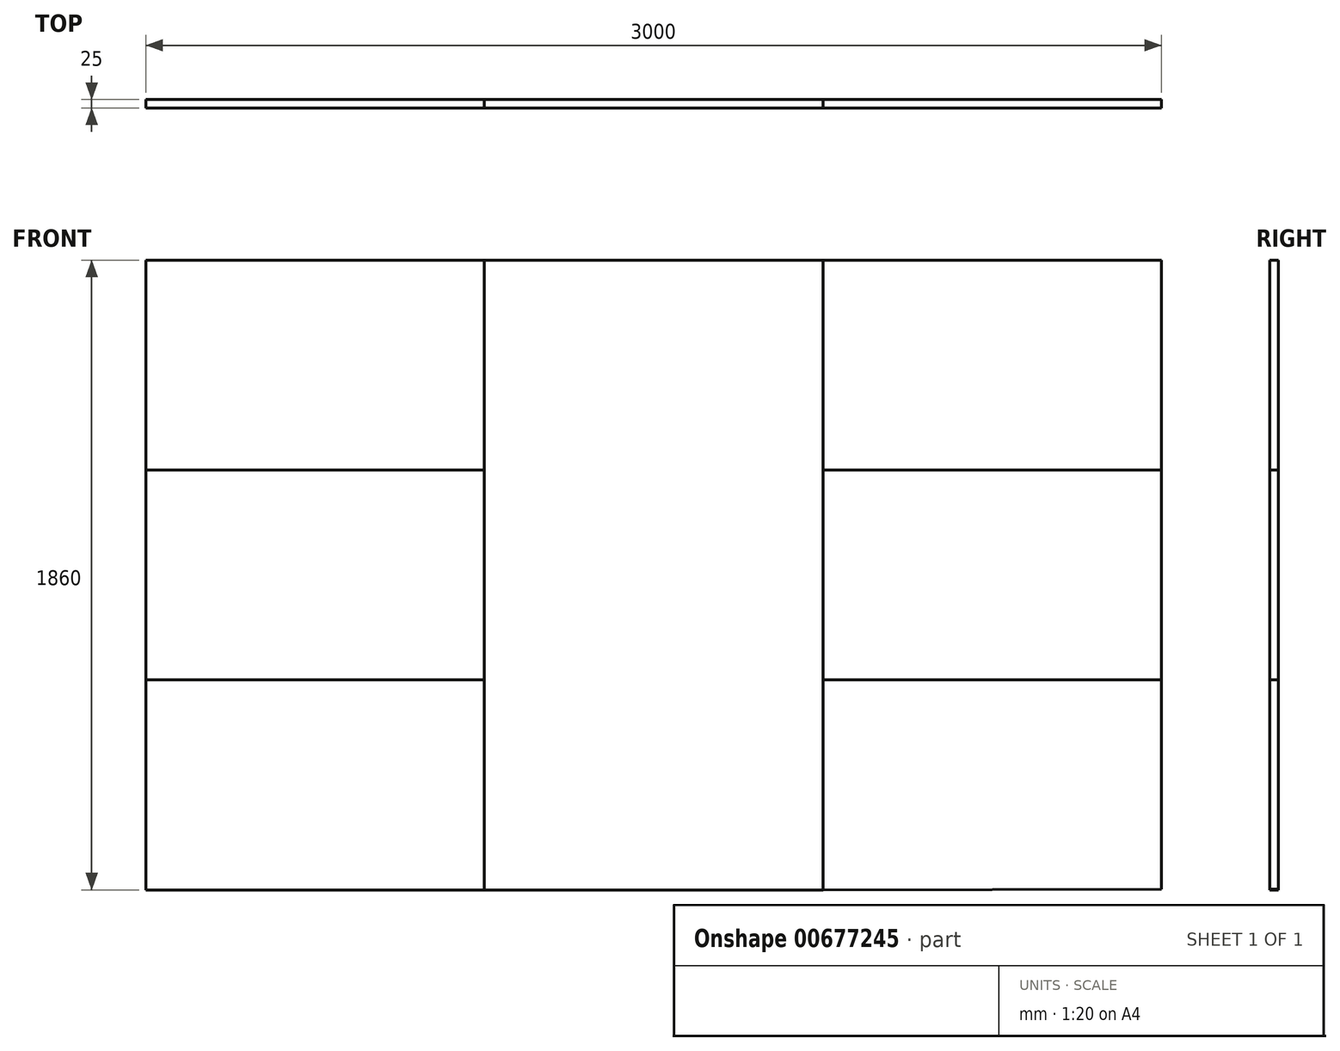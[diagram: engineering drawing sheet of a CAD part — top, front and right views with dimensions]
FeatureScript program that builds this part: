
annotation { "Feature Type Name" : "Feature", "Feature Type Description" : "" }
export const myFeature = defineFeature(function(context is Context, id is Id, definition is map)
    precondition{}
    {
        {
            var Q0;
            Q0=qCreatedBy(makeId("Front.planeOp"),FACE);
            var sketch = newSketch(context, id + "F0", { "sketchPlane" : qUnion([Q0])});
            skLineSegment(sketch, "E0.bottom", {"start": v(-857.14, 930) * mm, "end": v(1142.86, 930) * mm});
            skLineSegment(sketch, "E0.top", {"start": v(-857.14, -930) * mm, "end": v(1142.86, -930) * mm});
            skLineSegment(sketch, "E0.left", {"start": v(-857.14, 930) * mm, "end": v(-857.14, -930) * mm});
            skLineSegment(sketch, "E0.right", {"start": v(1142.86, 930) * mm, "end": v(1142.86, -930) * mm});
            skLineSegment(sketch, "E1", {"start": v(142.86, 930) * mm, "end": v(142.86, -930) * mm});
            skLineSegment(sketch, "E2", {"start": v(-857.14, 310) * mm, "end": v(142.86, 310) * mm});
            skLineSegment(sketch, "E3", {"start": v(-857.14, -310) * mm, "end": v(142.86, -310) * mm});
            skLineSegment(sketch, "E4", {"start": v(1142.86, 930) * mm, "end": v(2142.86, 930) * mm});
            skLineSegment(sketch, "E5", {"start": v(2142.86, 930) * mm, "end": v(2142.86, -928.17) * mm});
            skLineSegment(sketch, "E6", {"start": v(2142.86, -928.17) * mm, "end": v(1142.86, -930) * mm});
            skLineSegment(sketch, "E7", {"start": v(1142.86, -310) * mm, "end": v(2142.86, -310) * mm});
            skLineSegment(sketch, "E8", {"start": v(1142.86, 310) * mm, "end": v(2142.86, 310) * mm});
            skSolve(sketch);
        }
        {
            var Q0;
            Q0=sQuery(id+"F0.wireOp",EDGE,"E0.left");
            var Q1;
            Q1=sQuery(id+"F0.wireOp",EDGE,"E1");
            var Q2;
            Q2=sQuery(id+"F0.wireOp",EDGE,"E0.right");
            var Q3;
            Q3=sQuery(id+"F0.wireOp",EDGE,"E5");
            extrude(context, id + "F1", {"bodyType" : ToolBodyType.SURFACE, "surfaceEntities" : qUnion([Q0, Q1, Q2, Q3]), "depth" : 25 * mm, "offsetDistance" : 25 * mm});
        }
        {
            var Q0;
            Q0=sQuery(id+"F0.wireOp",EDGE,"E2");
            var Q1;
            Q1=sQuery(id+"F0.wireOp",EDGE,"E3");
            var Q2;
            Q2=sQuery(id+"F0.wireOp",EDGE,"E0.top");
            var Q3;
            Q3=sQuery(id+"F0.wireOp",EDGE,"E7");
            var Q4;
            Q4=sQuery(id+"F0.wireOp",EDGE,"E8");
            var Q5;
            Q5=sQuery(id+"F0.wireOp",EDGE,"E4");
            extrude(context, id + "F2", {"bodyType" : ToolBodyType.SURFACE, "surfaceEntities" : qUnion([Q0, Q1, Q2, Q3, Q4, Q5]), "depth" : 25 * mm, "offsetDistance" : 25 * mm});
        }
        {
            var Q0;
            Q0=sQuery(id+"F0.wireOp",EDGE,"E0.bottom");
            var Q1;
            Q1=sQuery(id+"F0.wireOp",EDGE,"E6");
            extrude(context, id + "F3", {"bodyType" : ToolBodyType.SURFACE, "surfaceEntities" : qUnion([Q0, Q1]), "depth" : 25 * mm, "offsetDistance" : 25 * mm});
        }
    });
